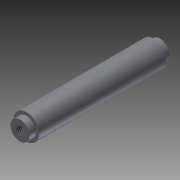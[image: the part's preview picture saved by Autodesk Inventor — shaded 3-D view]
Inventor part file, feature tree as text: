
AUTODESK INVENTOR PART (.ipt)
format: ipt  version: 2012 (Build 160160000, 160)  size: 91,648 bytes
history: native  units: in
note: dims shown in document units (in); Inventor stores cm internally (conversion verified against a paired STEP export)
features: extrude x4, sketch x3, thread x1
ambient origin geometry x8: Origin, YZ Plane, XZ Plane, XY Plane, X Axis, Y Axis, Z Axis, Center Point
bodies: Solid1 (feature_tree)
feature tree (8):
  extrude  "Extrusion1"  Depth=2.75in TaperAngle=0.0deg
  sketch  "Sketch6"  dims[d43=0.164in d44=0.375in]
  extrude  "Extrusion11"  Depth=0.375in
  extrude  "Extrusion12"  Depth=0.125in TaperAngle=0.0deg
  extrude  "Extrusion13"  Depth=0.125in TaperAngle=0.0deg
  thread  "Thread7"  [1 undecoded]
  sketch  "Sketch1"  dims[d0=0.5in d1=2.75in d2=0.0in]
  sketch  "Sketch7"  dims[d45=0.125in d46=0.0in d47=0.125in d48=0.0in d49=0.125in d50=0.0in d51=1.0in d52=0.0in]
note: 1 required parameter value undecoded (feature->parameter linkage not recoverable at this tier; creation-order binding heuristic only, values carry confidence <= 0.55)
